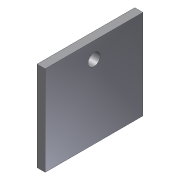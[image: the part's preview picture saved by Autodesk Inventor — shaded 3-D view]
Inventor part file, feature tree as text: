
AUTODESK INVENTOR PART (.ipt)
format: ipt  version: 2012 (Build 160160000, 160)  size: 76,288 bytes
history: native  units: in
note: dims shown in document units (in); Inventor stores cm internally (conversion verified against a paired STEP export)
features: extrude x1, sketch x1
ambient origin geometry x8: Origin, YZ Plane, XZ Plane, XY Plane, X Axis, Y Axis, Z Axis, Center Point
bodies: Solid1 (feature_tree)
feature tree (2):
  extrude  "Extrusion1"  Depth=2.75in
  sketch  "Sketch1"  dims[d0=3.0in d1=2.75in d2=1.5in d3=0.375in d4=0.5in d5=0.25in d6=0.0in]
